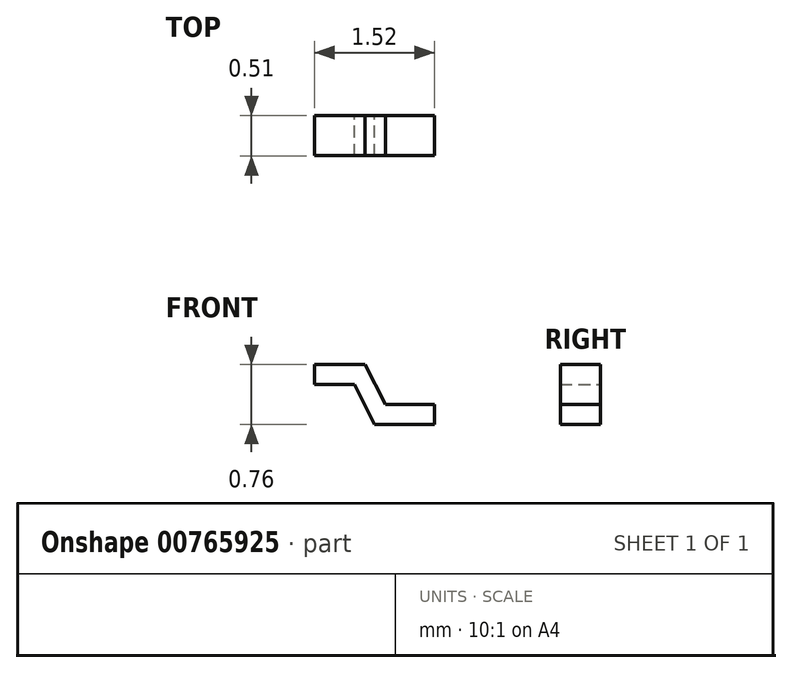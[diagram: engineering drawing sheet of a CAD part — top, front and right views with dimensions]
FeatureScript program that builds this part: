
annotation { "Feature Type Name" : "Feature", "Feature Type Description" : "" }
export const myFeature = defineFeature(function(context is Context, id is Id, definition is map)
    precondition{}
    {
        {
            var Q0;
            Q0=qCreatedBy(makeId("Front.planeOp"),FACE);
            var sketch = newSketch(context, id + "F0", { "sketchPlane" : qUnion([Q0])});
            skLineSegment(sketch, "E0", {"start": v(0, 0.76) * mm, "end": v(0.64, 0.76) * mm});
            skLineSegment(sketch, "E1", {"start": v(0.64, 0.76) * mm, "end": v(0.9, 0.25) * mm});
            skLineSegment(sketch, "E2", {"start": v(0.9, 0.25) * mm, "end": v(1.52, 0.25) * mm});
            skLineSegment(sketch, "E3", {"start": v(1.52, 0.25) * mm, "end": v(1.52, 0) * mm});
            skLineSegment(sketch, "E4", {"start": v(1.52, 0) * mm, "end": v(0.76, 0) * mm});
            skLineSegment(sketch, "E5", {"start": v(0.76, 0) * mm, "end": v(0.5, 0.5) * mm});
            skLineSegment(sketch, "E6", {"start": v(0.5, 0.5) * mm, "end": v(0, 0.5) * mm});
            skLineSegment(sketch, "E7", {"start": v(0, 0.5) * mm, "end": v(0, 0.76) * mm});
            skSolve(sketch);
        }
        {
            var Q0;
            Q0=makeQuery(id+"F0.imprint","IMPRINT",FACE,{"disambiguationData":[TD([[makeQuery(id+"F0.imprint","IMPRINT",EDGE,{"derivedFrom":sQuery(id+"F0.wireOp",EDGE,"E0")}),-1.0]])]});
            extrude(context, id + "F1", {"entities" : qUnion([Q0]), "depth" : 0.5 * mm, "offsetDistance" : 25.4 * mm});
        }
    });
